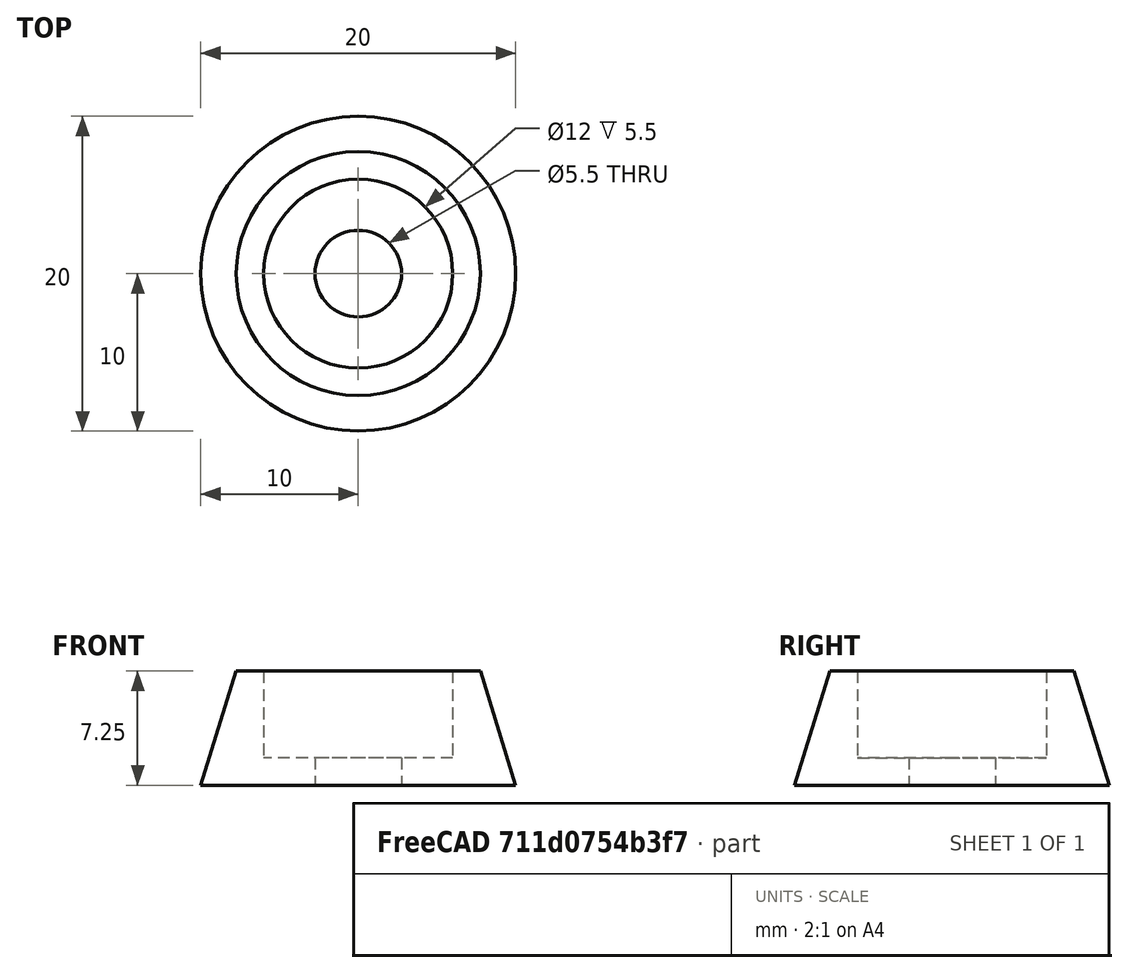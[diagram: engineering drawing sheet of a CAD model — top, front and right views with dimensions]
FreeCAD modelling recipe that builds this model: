
FCSTD DOCUMENT  (FreeCAD 0.18R4 (GitTag))
Label: frame_foot_v0.1
License: CreativeCommons Attribution-ShareAlike
LicenseURL: http://creativecommons.org/licenses/by-sa/4.0/
objects: Sketcher::SketchObject×1, PartDesign::Revolution×1, PartDesign::Body×1
note: 4 computed .brp shape members not serialized (recipe doc carries the construction recipe); baked Part::Feature solids carry a one-line shape summary decoded from their .brp

FEATURE [Sketcher::SketchObject] Sketch
  MapMode = 5
  Placement = pos=(0,0,0) rot=(1,0,0;1.5708rad)
  Support = -> [XZ_Plane]
  sketch-geometry (6):
    g0: LineSegment StartX=6 StartY=7.25 StartZ=0 EndX=6 EndY=1.75 EndZ=0
    g1: LineSegment StartX=6 StartY=1.75 StartZ=0 EndX=2.75 EndY=1.75 EndZ=0
    g2: LineSegment StartX=2.75 StartY=1.75 StartZ=0 EndX=2.75 EndY=0 EndZ=0
    g3: LineSegment StartX=2.75 StartY=0 StartZ=0 EndX=10 EndY=0 EndZ=0
    g4: LineSegment StartX=10 StartY=0 StartZ=0 EndX=7.75 EndY=7.25 EndZ=0
    g5: LineSegment StartX=7.75 StartY=7.25 StartZ=0 EndX=6 EndY=7.25 EndZ=0
  constraints (18):
    c: Coincident(g0,g1)
    c: Coincident(g1,g2)
    c: Coincident(g2,g3)
    c: Coincident(g3,g4)
    c: Coincident(g4,g5)
    c: Coincident(g0,g5)
    c: Horizontal(g3)
    c: Horizontal(g1)
    c: Horizontal(g5)
    c: Vertical(g2)
    c: Vertical(g0)
    c: PointOnObject(g2,g-1)
    c: DistanceX(g3) = 10
    c: DistanceX(g2) = 2.75
    c: DistanceY(g2,g2) = 1.75
    c: DistanceX(g1,g1) = 3.25
    c: DistanceY(g0,g0) = 5.5
    c: DistanceX(g5,g5) = 1.75
FEATURE [PartDesign::Revolution] Revolution
  Angle = 360
  Axis = (0,-1.035e-13,1)
  Base = (0,0,0)
  Placement = pos=(0,0,0) rot=(1,0,0;1.5708rad)
  Profile = -> Sketch
  ReferenceAxis = -> Sketch [V_Axis]
  Reversed = true
FEATURE [PartDesign::Body] Body
  Group = -> [Sketch,Revolution]
  Origin = -> Origin
  Tip = -> Revolution
